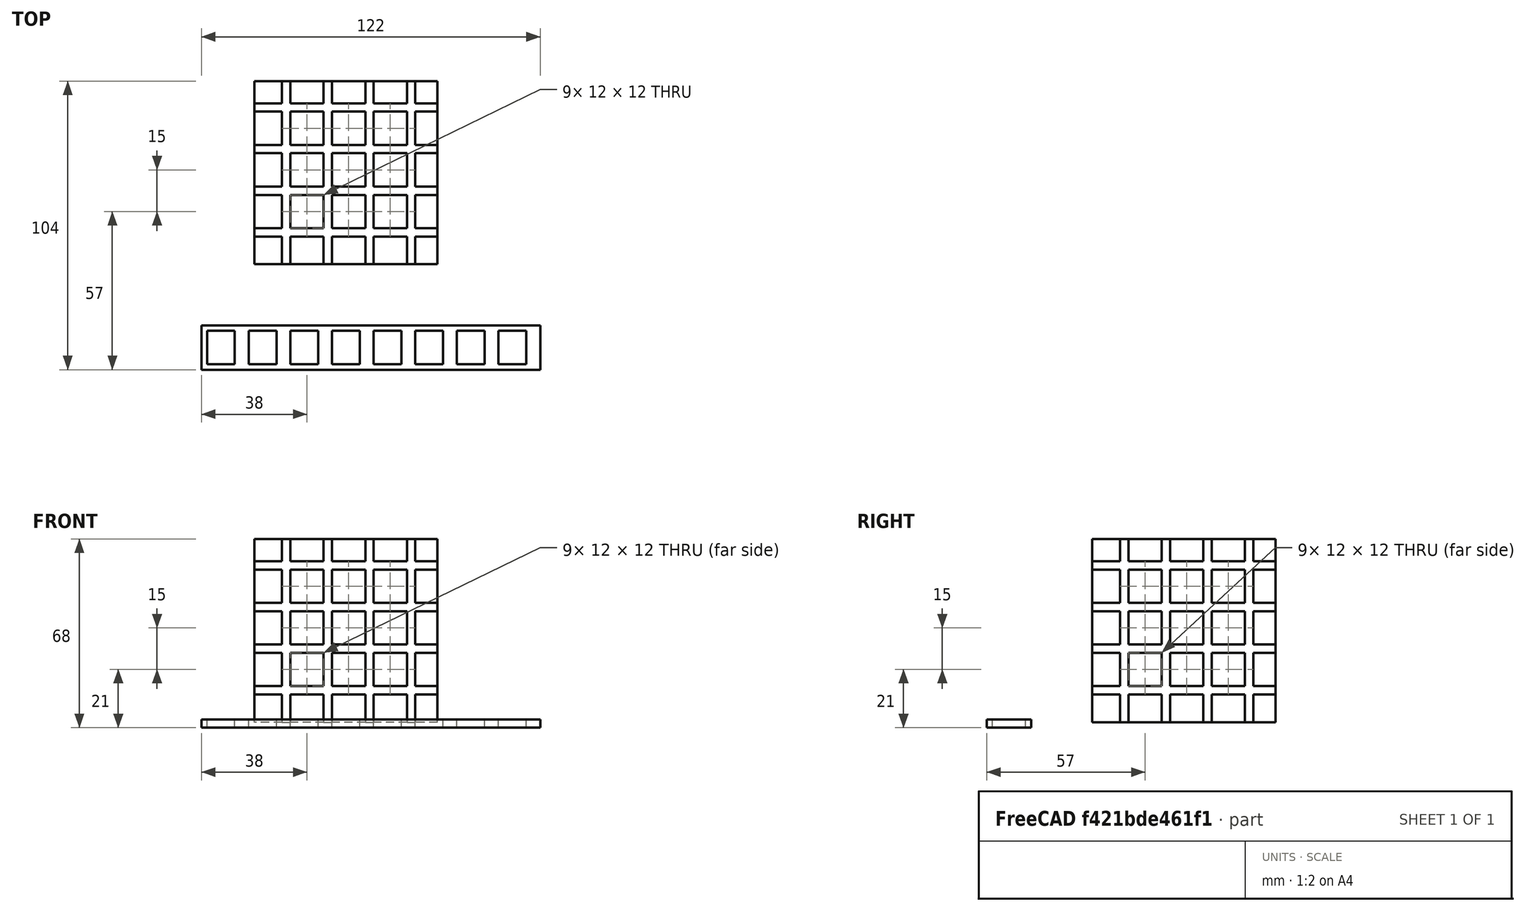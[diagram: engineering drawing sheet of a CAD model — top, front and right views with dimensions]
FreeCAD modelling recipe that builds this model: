
FCSTD DOCUMENT  (FreeCAD 0.16R6707 (Git))
Label: Array
License: CreativeCommons Attribution-ShareAlike
LicenseURL: http://creativecommons.org/licenses/by-sa/4.0/
objects: Part::Box×4, Part::FeaturePython×2, Part::Cut×2
note: 8 computed .brp shape members not serialized (recipe doc carries the construction recipe); baked Part::Feature solids carry a one-line shape summary decoded from their .brp

FEATURE [Part::Box] Box  label="MAster_box"
  Height = 10
  Length = 10
  Placement = pos=(0,-1,0) rot=(0,0,1;0rad)
  Width = 12
FEATURE [Part::FeaturePython] Array  # Draft array (typed FeaturePython)
  Angle = 360
  ArrayType = 0
  Axis = (0,0,1)
  Base = -> Box
  Center = (0,0,0)
  Fuse = false
  IntervalAxis = (0,0,0)
  IntervalX = (15,0,0)
  IntervalY = (0,1,0)
  IntervalZ = (0,0,0)
  NumberPolar = 1
  NumberX = 8
  NumberY = 1
  NumberZ = 1
FEATURE [Part::Box] Box001  label="Base"
  Height = 3
  Length = 122
  Placement = pos=(-2,-3,0) rot=(0,0,1;0rad)
  Width = 16
FEATURE [Part::Cut] Cut
  Base = -> Box001
  Placement = pos=(-15,-33,0) rot=(0,0,1;0rad)
  Tool = -> Array
FEATURE [Part::Box] Box002  label="Cubo_master"
  Height = 12
  Length = 12
  Width = 12
FEATURE [Part::FeaturePython] Array001  # Draft array (typed FeaturePython)
  Angle = 360
  ArrayType = 0
  Axis = (0,0,1)
  Base = -> Box002
  Center = (0,0,0)
  Fuse = false
  IntervalAxis = (0,0,0)
  IntervalX = (15,0,0)
  IntervalY = (0,15,0)
  IntervalZ = (0,0,15)
  NumberPolar = 1
  NumberX = 5
  NumberY = 5
  NumberZ = 5
FEATURE [Part::Box] Box003  label="Cubo_base"
  Height = 66
  Length = 66
  Placement = pos=(2,2,2) rot=(0,0,1;0rad)
  Width = 66
FEATURE [Part::Cut] Cut001  label="Caja"
  Base = -> Box003
  Tool = -> Array001
